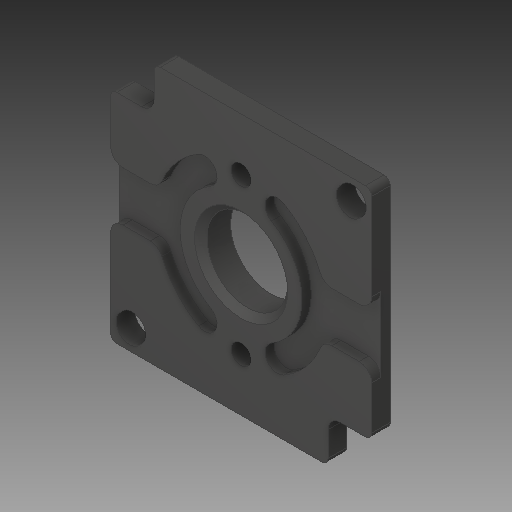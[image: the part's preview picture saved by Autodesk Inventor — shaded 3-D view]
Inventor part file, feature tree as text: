
AUTODESK INVENTOR PART (.ipt)
format: ipt  version: 2017 SP1 (Build 210196100, 196)  size: 265,216 bytes
history: native  units: in
note: dims shown in document units (in); Inventor stores cm internally (conversion verified against a paired STEP export)
features: fillet x1
ambient origin geometry x8: Origin, YZ Plane, XZ Plane, XY Plane, X Axis, Y Axis, Z Axis, Center Point
bodies: Solid1 (feature_tree)
feature tree (1):
  fillet  "Fillet4"  [1 undecoded]
note: 1 required parameter value undecoded (feature->parameter linkage not recoverable at this tier; creation-order binding heuristic only, values carry confidence <= 0.55)
